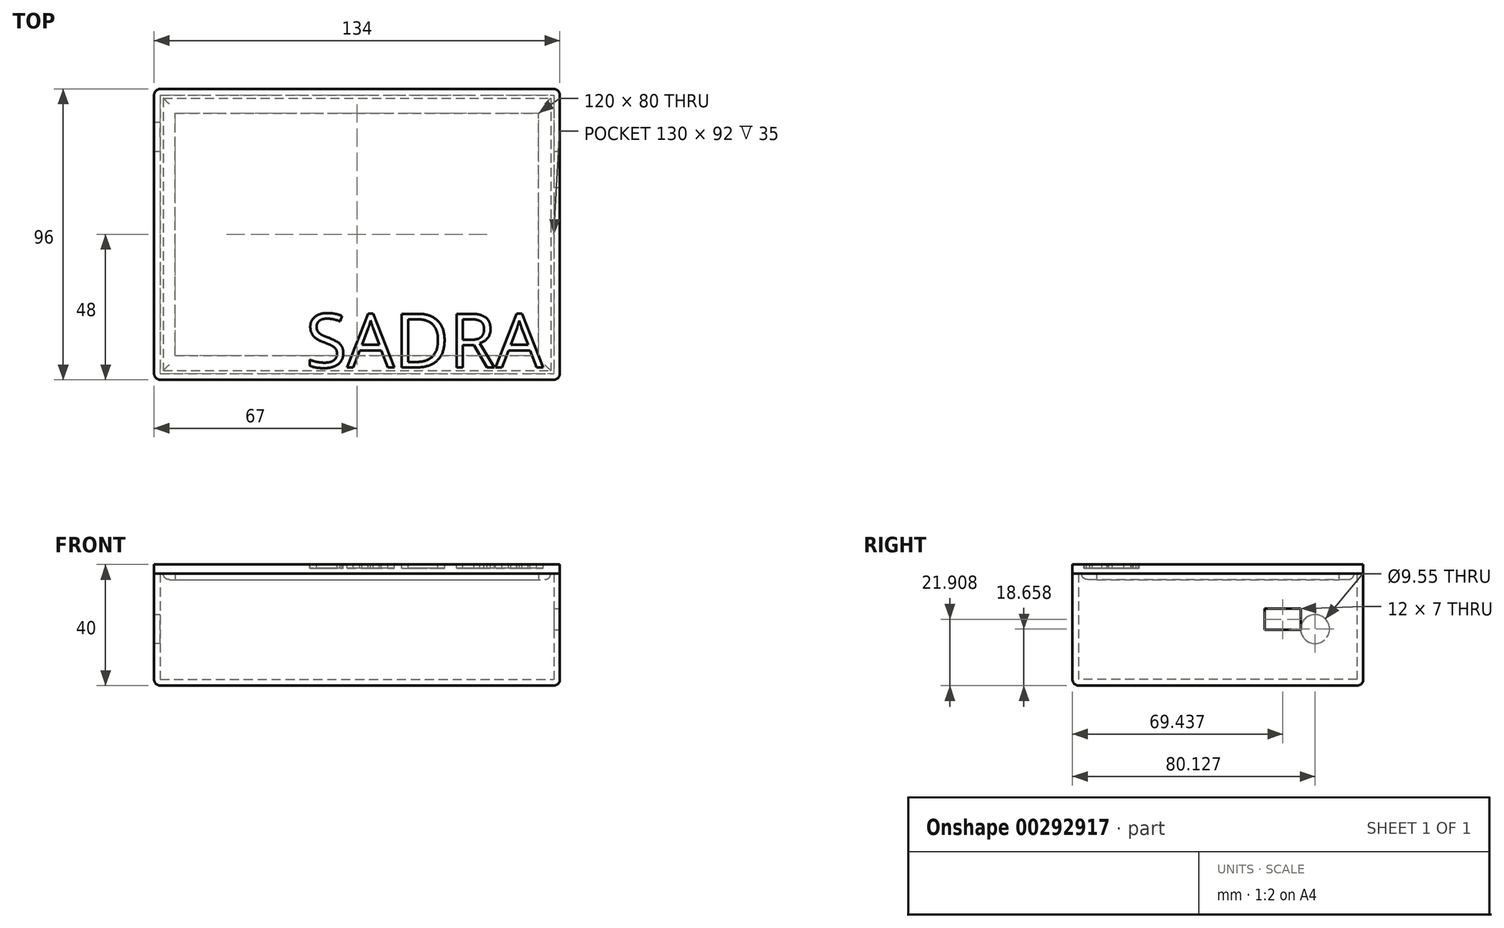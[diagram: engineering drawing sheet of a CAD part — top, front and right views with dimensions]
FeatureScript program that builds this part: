
annotation { "Feature Type Name" : "Feature", "Feature Type Description" : "" }
export const myFeature = defineFeature(function(context is Context, id is Id, definition is map)
    precondition{}
    {
        {
            var Q0;
            Q0=qCreatedBy(makeId("Top.planeOp"),FACE);
            var sketch = newSketch(context, id + "F0", { "sketchPlane" : qUnion([Q0])});
            skLineSegment(sketch, "E0.bottom", {"start": v(-65, 46) * mm, "end": v(65, 46) * mm});
            skLineSegment(sketch, "E0.top", {"start": v(-65, -46) * mm, "end": v(65, -46) * mm});
            skLineSegment(sketch, "E0.left", {"start": v(-65, 46) * mm, "end": v(-65, -46) * mm});
            skLineSegment(sketch, "E0.right", {"start": v(65, 46) * mm, "end": v(65, -46) * mm});
            skPoint(sketch, "E0.middle", {"position": v(0, 0) * mm});
            skLineSegment(sketch, "E1.bottom", {"start": v(-67, 48) * mm, "end": v(67, 48) * mm});
            skLineSegment(sketch, "E1.top", {"start": v(-67, -48) * mm, "end": v(67, -48) * mm});
            skLineSegment(sketch, "E1.left", {"start": v(-67, 48) * mm, "end": v(-67, -48) * mm});
            skLineSegment(sketch, "E1.right", {"start": v(67, 48) * mm, "end": v(67, -48) * mm});
            skSolve(sketch);
        }
        {
            var Q0;
            Q0 = qSketchRegion(id + "F0", true);
            extrude(context, id + "F1", {"entities" : qUnion([Q0]), "depth" : 35 * mm});
        }
        {
            var Q0;
            Q0=makeQuery(id+"F1.opExtrude","CAP_FACE",FACE,{"disambiguationData":[OSD([sQuery(id+"F0.wireOp",EDGE,"E0.bottom"),sQuery(id+"F0.wireOp",EDGE,"E0.top"),sQuery(id+"F0.wireOp",EDGE,"E0.left"),sQuery(id+"F0.wireOp",EDGE,"E0.right"),sQuery(id+"F0.wireOp",EDGE,"E1.bottom"),sQuery(id+"F0.wireOp",EDGE,"E1.top"),sQuery(id+"F0.wireOp",EDGE,"E1.left"),sQuery(id+"F0.wireOp",EDGE,"E1.right")])],"isStart":true});
            var sketch = newSketch(context, id + "F2", { "sketchPlane" : qUnion([Q0])});
            skLineSegment(sketch, "E2.bottom", {"start": v(-67, 48) * mm, "end": v(67, 48) * mm});
            skLineSegment(sketch, "E2.top", {"start": v(-67, -48) * mm, "end": v(67, -48) * mm});
            skLineSegment(sketch, "E2.left", {"start": v(-67, 48) * mm, "end": v(-67, -48) * mm});
            skLineSegment(sketch, "E2.right", {"start": v(67, 48) * mm, "end": v(67, -48) * mm});
            skSolve(sketch);
        }
        {
            var Q0;
            Q0 = qSketchRegion(id + "F2", true);
            extrude(context, id + "F3", {"entities" : qUnion([Q0]), "operationType" : NewBodyOperationType.ADD, "depth" : 2 * mm});
        }
        {
            var Q0;
            Q0=makeQuery(id+"F3.boolean.opBoolean","MERGE",EDGE,{"derivedFrom":[makeQuery(id+"F1.opExtrude","SWEPT_EDGE",EDGE,{"disambiguationData":[OSD([sQuery(id+"F0.wireOp",EDGE,"E1.top"),sQuery(id+"F0.wireOp",EDGE,"E1.left")])]}),makeQuery(id+"F3.opExtrude","SWEPT_EDGE",EDGE,{"disambiguationData":[OSD([sQuery(id+"F2.wireOp",EDGE,"E2.bottom"),sQuery(id+"F2.wireOp",EDGE,"E2.left")])]})]});
            var Q1;
            Q1=makeQuery(id+"F3.boolean.opBoolean","MERGE",EDGE,{"derivedFrom":[makeQuery(id+"F1.opExtrude","SWEPT_EDGE",EDGE,{"disambiguationData":[OSD([sQuery(id+"F0.wireOp",EDGE,"E1.top"),sQuery(id+"F0.wireOp",EDGE,"E1.right")])]}),makeQuery(id+"F3.opExtrude","SWEPT_EDGE",EDGE,{"disambiguationData":[OSD([sQuery(id+"F2.wireOp",EDGE,"E2.bottom"),sQuery(id+"F2.wireOp",EDGE,"E2.right")])]})]});
            var Q2;
            Q2=makeQuery(id+"F3.boolean.opBoolean","MERGE",EDGE,{"derivedFrom":[makeQuery(id+"F1.opExtrude","SWEPT_EDGE",EDGE,{"disambiguationData":[OSD([sQuery(id+"F0.wireOp",EDGE,"E1.bottom"),sQuery(id+"F0.wireOp",EDGE,"E1.right")])]}),makeQuery(id+"F3.opExtrude","SWEPT_EDGE",EDGE,{"disambiguationData":[OSD([sQuery(id+"F2.wireOp",EDGE,"E2.top"),sQuery(id+"F2.wireOp",EDGE,"E2.right")])]})]});
            var Q3;
            Q3=makeQuery(id+"F3.boolean.opBoolean","MERGE",EDGE,{"derivedFrom":[makeQuery(id+"F1.opExtrude","SWEPT_EDGE",EDGE,{"disambiguationData":[OSD([sQuery(id+"F0.wireOp",EDGE,"E1.bottom"),sQuery(id+"F0.wireOp",EDGE,"E1.left")])]}),makeQuery(id+"F3.opExtrude","SWEPT_EDGE",EDGE,{"disambiguationData":[OSD([sQuery(id+"F2.wireOp",EDGE,"E2.top"),sQuery(id+"F2.wireOp",EDGE,"E2.left")])]})]});
            fillet(context, id + "F4", {"entities" : qUnion([Q0, Q1, Q2, Q3]), "radius" : 2 * mm, "tangentPropagation" : true, "allowEdgeOverflow" : false});
        }
        {
            var Q0;
            Q0=makeQuery(id+"F3.opExtrude","CAP_EDGE",EDGE,{"disambiguationData":[OSD([sQuery(id+"F2.wireOp",EDGE,"E2.bottom")])],"isStart":false});
            var Q1;
            Q1=makeQuery(id+"F3.opExtrude","CAP_EDGE",EDGE,{"disambiguationData":[OSD([sQuery(id+"F2.wireOp",EDGE,"E2.left")])],"isStart":false});
            var Q2;
            {var subQ0=sQuery(id+"F2.wireOp",EDGE,"E2.left");var subQ1=sQuery(id+"F2.wireOp",EDGE,"E2.bottom");Q2=makeQuery(id+"F4.opFillet","BLEND_EDGE",EDGE,{"blendedFrom":[makeQuery(id+"F3.boolean.opBoolean","MERGE",EDGE,{"derivedFrom":[makeQuery(id+"F1.opExtrude","SWEPT_EDGE",EDGE,{"disambiguationData":[OSD([sQuery(id+"F0.wireOp",EDGE,"E1.top"),sQuery(id+"F0.wireOp",EDGE,"E1.left")])]}),makeQuery(id+"F3.opExtrude","SWEPT_EDGE",EDGE,{"disambiguationData":[OSD([subQ1,subQ0])]})]}),makeQuery(id+"F3.opExtrude","CAP_FACE",FACE,{"disambiguationData":[OSD([subQ1,sQuery(id+"F2.wireOp",EDGE,"E2.top"),subQ0,sQuery(id+"F2.wireOp",EDGE,"E2.right")])],"isStart":false})],"blendedInto":[makeQuery(id+"F3.opExtrude","CAP_FACE",FACE,{"disambiguationData":[OSD([subQ1,sQuery(id+"F2.wireOp",EDGE,"E2.top"),subQ0,sQuery(id+"F2.wireOp",EDGE,"E2.right")])],"isStart":false})]});}
            var Q3;
            {var subQ0=sQuery(id+"F2.wireOp",EDGE,"E2.left");var subQ1=sQuery(id+"F2.wireOp",EDGE,"E2.top");Q3=makeQuery(id+"F4.opFillet","BLEND_EDGE",EDGE,{"blendedFrom":[makeQuery(id+"F3.boolean.opBoolean","MERGE",EDGE,{"derivedFrom":[makeQuery(id+"F1.opExtrude","SWEPT_EDGE",EDGE,{"disambiguationData":[OSD([sQuery(id+"F0.wireOp",EDGE,"E1.bottom"),sQuery(id+"F0.wireOp",EDGE,"E1.left")])]}),makeQuery(id+"F3.opExtrude","SWEPT_EDGE",EDGE,{"disambiguationData":[OSD([subQ1,subQ0])]})]}),makeQuery(id+"F3.opExtrude","CAP_FACE",FACE,{"disambiguationData":[OSD([sQuery(id+"F2.wireOp",EDGE,"E2.bottom"),subQ1,subQ0,sQuery(id+"F2.wireOp",EDGE,"E2.right")])],"isStart":false})],"blendedInto":[makeQuery(id+"F3.opExtrude","CAP_FACE",FACE,{"disambiguationData":[OSD([sQuery(id+"F2.wireOp",EDGE,"E2.bottom"),subQ1,subQ0,sQuery(id+"F2.wireOp",EDGE,"E2.right")])],"isStart":false})]});}
            var Q4;
            Q4=makeQuery(id+"F3.opExtrude","CAP_EDGE",EDGE,{"disambiguationData":[OSD([sQuery(id+"F2.wireOp",EDGE,"E2.top")])],"isStart":false});
            var Q5;
            {var subQ0=sQuery(id+"F2.wireOp",EDGE,"E2.right");var subQ1=sQuery(id+"F2.wireOp",EDGE,"E2.top");Q5=makeQuery(id+"F4.opFillet","BLEND_EDGE",EDGE,{"blendedFrom":[makeQuery(id+"F3.boolean.opBoolean","MERGE",EDGE,{"derivedFrom":[makeQuery(id+"F1.opExtrude","SWEPT_EDGE",EDGE,{"disambiguationData":[OSD([sQuery(id+"F0.wireOp",EDGE,"E1.bottom"),sQuery(id+"F0.wireOp",EDGE,"E1.right")])]}),makeQuery(id+"F3.opExtrude","SWEPT_EDGE",EDGE,{"disambiguationData":[OSD([subQ1,subQ0])]})]}),makeQuery(id+"F3.opExtrude","CAP_FACE",FACE,{"disambiguationData":[OSD([sQuery(id+"F2.wireOp",EDGE,"E2.bottom"),subQ1,sQuery(id+"F2.wireOp",EDGE,"E2.left"),subQ0])],"isStart":false})],"blendedInto":[makeQuery(id+"F3.opExtrude","CAP_FACE",FACE,{"disambiguationData":[OSD([sQuery(id+"F2.wireOp",EDGE,"E2.bottom"),subQ1,sQuery(id+"F2.wireOp",EDGE,"E2.left"),subQ0])],"isStart":false})]});}
            var Q6;
            Q6=makeQuery(id+"F3.opExtrude","CAP_EDGE",EDGE,{"disambiguationData":[OSD([sQuery(id+"F2.wireOp",EDGE,"E2.right")])],"isStart":false});
            var Q7;
            {var subQ0=sQuery(id+"F2.wireOp",EDGE,"E2.right");var subQ1=sQuery(id+"F2.wireOp",EDGE,"E2.bottom");Q7=makeQuery(id+"F4.opFillet","BLEND_EDGE",EDGE,{"blendedFrom":[makeQuery(id+"F3.boolean.opBoolean","MERGE",EDGE,{"derivedFrom":[makeQuery(id+"F1.opExtrude","SWEPT_EDGE",EDGE,{"disambiguationData":[OSD([sQuery(id+"F0.wireOp",EDGE,"E1.top"),sQuery(id+"F0.wireOp",EDGE,"E1.right")])]}),makeQuery(id+"F3.opExtrude","SWEPT_EDGE",EDGE,{"disambiguationData":[OSD([subQ1,subQ0])]})]}),makeQuery(id+"F3.opExtrude","CAP_FACE",FACE,{"disambiguationData":[OSD([subQ1,sQuery(id+"F2.wireOp",EDGE,"E2.top"),sQuery(id+"F2.wireOp",EDGE,"E2.left"),subQ0])],"isStart":false})],"blendedInto":[makeQuery(id+"F3.opExtrude","CAP_FACE",FACE,{"disambiguationData":[OSD([subQ1,sQuery(id+"F2.wireOp",EDGE,"E2.top"),sQuery(id+"F2.wireOp",EDGE,"E2.left"),subQ0])],"isStart":false})]});}
            fillet(context, id + "F5", {"entities" : qUnion([Q0, Q1, Q2, Q3, Q4, Q5, Q6, Q7]), "radius" : 2 * mm, "tangentPropagation" : true, "allowEdgeOverflow" : false});
        }
        {
            var Q0;
            Q0=makeQuery(id+"F3.boolean.opBoolean","MERGE",FACE,{"derivedFrom":[makeQuery(id+"F1.opExtrude","SWEPT_FACE",FACE,{"disambiguationData":[OSD([sQuery(id+"F0.wireOp",EDGE,"E1.left")])]}),makeQuery(id+"F3.opExtrude","SWEPT_FACE",FACE,{"disambiguationData":[OSD([sQuery(id+"F2.wireOp",EDGE,"E2.left")])]})]});
            var sketch = newSketch(context, id + "F6", { "sketchPlane" : qUnion([Q0])});
            skCircle(sketch, "E3", {"center": v(-32.13, 16.66) * mm, "radius": 4.78 * mm});
            skSolve(sketch);
        }
        {
            var Q0;
            Q0 = qSketchRegion(id + "F6", true);
            extrude(context, id + "F7", {"entities" : qUnion([Q0]), "operationType" : NewBodyOperationType.REMOVE, "oppositeDirection" : true, "depth" : 25 * mm});
        }
        {
            var Q0;
            Q0=makeQuery(id+"F3.boolean.opBoolean","MERGE",FACE,{"derivedFrom":[makeQuery(id+"F1.opExtrude","SWEPT_FACE",FACE,{"disambiguationData":[OSD([sQuery(id+"F0.wireOp",EDGE,"E1.right")])]}),makeQuery(id+"F3.opExtrude","SWEPT_FACE",FACE,{"disambiguationData":[OSD([sQuery(id+"F2.wireOp",EDGE,"E2.right")])]})]});
            var sketch = newSketch(context, id + "F8", { "sketchPlane" : qUnion([Q0])});
            skLineSegment(sketch, "E4.bottom", {"start": v(27.44, 23.4) * mm, "end": v(15.44, 23.4) * mm});
            skLineSegment(sketch, "E4.top", {"start": v(27.44, 16.4) * mm, "end": v(15.44, 16.4) * mm});
            skLineSegment(sketch, "E4.left", {"start": v(27.44, 23.4) * mm, "end": v(27.44, 16.4) * mm});
            skLineSegment(sketch, "E4.right", {"start": v(15.44, 23.4) * mm, "end": v(15.44, 16.4) * mm});
            skSolve(sketch);
        }
        {
            var Q0;
            Q0 = qSketchRegion(id + "F8", true);
            extrude(context, id + "F9", {"entities" : qUnion([Q0]), "operationType" : NewBodyOperationType.REMOVE, "oppositeDirection" : true, "depth" : 25 * mm});
        }
        {
            var Q0;
            Q0=makeQuery(id+"F1.opExtrude","CAP_FACE",FACE,{"disambiguationData":[OSD([sQuery(id+"F0.wireOp",EDGE,"E0.bottom"),sQuery(id+"F0.wireOp",EDGE,"E0.top"),sQuery(id+"F0.wireOp",EDGE,"E0.left"),sQuery(id+"F0.wireOp",EDGE,"E0.right"),sQuery(id+"F0.wireOp",EDGE,"E1.bottom"),sQuery(id+"F0.wireOp",EDGE,"E1.top"),sQuery(id+"F0.wireOp",EDGE,"E1.left"),sQuery(id+"F0.wireOp",EDGE,"E1.right")])],"isStart":false});
            var sketch = newSketch(context, id + "F10", { "sketchPlane" : qUnion([Q0])});
            skLineSegment(sketch, "E5.bottom", {"start": v(-81.8, 54.97) * mm, "end": v(85.87, 54.97) * mm});
            skLineSegment(sketch, "E5.top", {"start": v(-81.8, -58.3) * mm, "end": v(85.87, -58.3) * mm});
            skLineSegment(sketch, "E5.left", {"start": v(-81.8, 54.97) * mm, "end": v(-81.8, -58.3) * mm});
            skLineSegment(sketch, "E5.right", {"start": v(85.87, 54.97) * mm, "end": v(85.87, -58.3) * mm});
            skLineSegment(sketch, "E6.0.0", {"start": v(-67, 46) * mm, "end": v(-67, -46) * mm});
            skArc(sketch, "E6.0.1", {"start": v(-67, -46) * mm, "mid": v(-66.41, -47.41) * mm, "end": v(-65, -48) * mm});
            skLineSegment(sketch, "E6.0.2", {"start": v(-65, -48) * mm, "end": v(65, -48) * mm});
            skArc(sketch, "E6.0.3", {"start": v(65, -48) * mm, "mid": v(66.41, -47.41) * mm, "end": v(67, -46) * mm});
            skLineSegment(sketch, "E6.0.4", {"start": v(67, -46) * mm, "end": v(67, 46) * mm});
            skArc(sketch, "E6.0.5", {"start": v(67, 46) * mm, "mid": v(66.41, 47.41) * mm, "end": v(65, 48) * mm});
            skLineSegment(sketch, "E6.0.6", {"start": v(65, 48) * mm, "end": v(-65, 48) * mm});
            skArc(sketch, "E6.0.7", {"start": v(-65, 48) * mm, "mid": v(-66.41, 47.41) * mm, "end": v(-67, 46) * mm});
            skSolve(sketch);
        }
        {
            var Q0;
            Q0=makeQuery(id+"F10.imprint","IMPRINT",FACE,{"disambiguationData":[TD([[makeQuery(id+"F10.imprint","IMPRINT",EDGE,{"derivedFrom":sQuery(id+"F10.wireOp",EDGE,"E6.0.0")}),1.0]])]});
            var Q1;
            Q1=makeQuery(id+"F10.imprint","IMPRINT",FACE,{"disambiguationData":[TD([[makeQuery(id+"F10.imprint","IMPRINT",EDGE,{"derivedFrom":makeQuery(id+"F1.opExtrude","CAP_EDGE",EDGE,{"disambiguationData":[OSD([sQuery(id+"F0.wireOp",EDGE,"E0.bottom")])],"isStart":false})}),-1.0]])]});
            extrude(context, id + "F11", {"entities" : qUnion([Q0, Q1]), "depth" : 3 * mm});
        }
        {
            var Q0;
            Q0=makeQuery(id+"F1.opExtrude","CAP_FACE",FACE,{"disambiguationData":[OSD([sQuery(id+"F0.wireOp",EDGE,"E0.bottom"),sQuery(id+"F0.wireOp",EDGE,"E0.top"),sQuery(id+"F0.wireOp",EDGE,"E0.left"),sQuery(id+"F0.wireOp",EDGE,"E0.right"),sQuery(id+"F0.wireOp",EDGE,"E1.bottom"),sQuery(id+"F0.wireOp",EDGE,"E1.top"),sQuery(id+"F0.wireOp",EDGE,"E1.left"),sQuery(id+"F0.wireOp",EDGE,"E1.right")])],"isStart":false});
            var sketch = newSketch(context, id + "F12", { "sketchPlane" : qUnion([Q0])});
            skLineSegment(sketch, "E7.bottom", {"start": v(-65, 46) * mm, "end": v(65, 46) * mm});
            skLineSegment(sketch, "E7.top", {"start": v(-65, -46) * mm, "end": v(65, -46) * mm});
            skLineSegment(sketch, "E7.left", {"start": v(-65, 46) * mm, "end": v(-65, -46) * mm});
            skLineSegment(sketch, "E7.right", {"start": v(65, 46) * mm, "end": v(65, -46) * mm});
            skSolve(sketch);
        }
        {
            var Q0;
            Q0=makeQuery(id+"F12.imprint","IMPRINT",FACE,{"disambiguationData":[TD([[makeQuery(id+"F12.imprint","IMPRINT",EDGE,{"derivedFrom":sQuery(id+"F12.wireOp",EDGE,"E7.bottom")}),-1.0]])]});
            var sketch = newSketch(context, id + "F13", { "sketchPlane" : qUnion([Q0])});
            skLineSegment(sketch, "E8.bottom", {"start": v(-64, 45) * mm, "end": v(64, 45) * mm});
            skLineSegment(sketch, "E8.top", {"start": v(-64, -45) * mm, "end": v(64, -45) * mm});
            skLineSegment(sketch, "E8.left", {"start": v(-64, 45) * mm, "end": v(-64, -45) * mm});
            skLineSegment(sketch, "E8.right", {"start": v(64, 45) * mm, "end": v(64, -45) * mm});
            skPoint(sketch, "E8.middle", {"position": v(0, 0) * mm});
            skSolve(sketch);
        }
        {
            var Q0;
            Q0 = qSketchRegion(id + "F13", true);
            extrude(context, id + "F14", {"entities" : qUnion([Q0]), "oppositeDirection" : true, "depth" : 2 * mm});
        }
        {
            var Q0;
            Q0=makeQuery(id+"F14.opExtrude","CAP_EDGE",EDGE,{"disambiguationData":[OSD([sQuery(id+"F13.wireOp",EDGE,"E8.bottom")])],"isStart":false});
            var Q1;
            Q1=makeQuery(id+"F14.opExtrude","CAP_EDGE",EDGE,{"disambiguationData":[OSD([sQuery(id+"F13.wireOp",EDGE,"E8.left")])],"isStart":false});
            var Q2;
            Q2=makeQuery(id+"F14.opExtrude","CAP_EDGE",EDGE,{"disambiguationData":[OSD([sQuery(id+"F13.wireOp",EDGE,"E8.top")])],"isStart":false});
            var Q3;
            Q3=makeQuery(id+"F14.opExtrude","CAP_EDGE",EDGE,{"disambiguationData":[OSD([sQuery(id+"F13.wireOp",EDGE,"E8.right")])],"isStart":false});
            fillet(context, id + "F15", {"entities" : qUnion([Q0, Q1, Q2, Q3]), "radius" : 2 * mm, "tangentPropagation" : true, "allowEdgeOverflow" : false});
        }
        {
            var Q0;
            Q0=makeQuery(id+"F14.opExtrude","CAP_FACE",FACE,{"disambiguationData":[OSD([sQuery(id+"F13.wireOp",EDGE,"E8.bottom"),sQuery(id+"F13.wireOp",EDGE,"E8.top"),sQuery(id+"F13.wireOp",EDGE,"E8.left"),sQuery(id+"F13.wireOp",EDGE,"E8.right")])],"isStart":false});
            var sketch = newSketch(context, id + "F16", { "sketchPlane" : qUnion([Q0])});
            skLineSegment(sketch, "E9.bottom", {"start": v(-60, 40) * mm, "end": v(60, 40) * mm});
            skLineSegment(sketch, "E9.top", {"start": v(-60, -40) * mm, "end": v(60, -40) * mm});
            skLineSegment(sketch, "E9.left", {"start": v(-60, 40) * mm, "end": v(-60, -40) * mm});
            skLineSegment(sketch, "E9.right", {"start": v(60, 40) * mm, "end": v(60, -40) * mm});
            skPoint(sketch, "E9.middle", {"position": v(0, 0) * mm});
            skSolve(sketch);
        }
        {
            var Q0;
            Q0 = qSketchRegion(id + "F16", true);
            extrude(context, id + "F17", {"entities" : qUnion([Q0]), "operationType" : NewBodyOperationType.REMOVE, "oppositeDirection" : true, "depth" : 2 * mm});
        }
        {
            var Q0;
            Q0=makeQuery(id+"F11.opExtrude","CAP_FACE",FACE,{"disambiguationData":[OSD([sQuery(id+"F10.wireOp",EDGE,"E6.0.0"),sQuery(id+"F10.wireOp",EDGE,"E6.0.1"),sQuery(id+"F10.wireOp",EDGE,"E6.0.2"),sQuery(id+"F10.wireOp",EDGE,"E6.0.3"),sQuery(id+"F10.wireOp",EDGE,"E6.0.4"),sQuery(id+"F10.wireOp",EDGE,"E6.0.5"),sQuery(id+"F10.wireOp",EDGE,"E6.0.6"),sQuery(id+"F10.wireOp",EDGE,"E6.0.7")])],"isStart":false});
            var sketch = newSketch(context, id + "F18", { "sketchPlane" : qUnion([Q0])});
            skText(sketch, "E10", { "text": "SADRA", "fontName": "OpenSans-Regular.ttf"});
            const initialGuessF18  = {"E10": [-0.01693, -0.04394, 1, 0, 0.01785]};
            skSetInitialGuess(sketch, initialGuessF18);
            skSolve(sketch);
        }
        {
            var Q0;
            Q0 = qSketchRegion(id + "F18", true);
            extrude(context, id + "F19", {"entities" : qUnion([Q0]), "operationType" : NewBodyOperationType.REMOVE, "oppositeDirection" : true, "depth" : 1.2 * mm});
        }
    });
